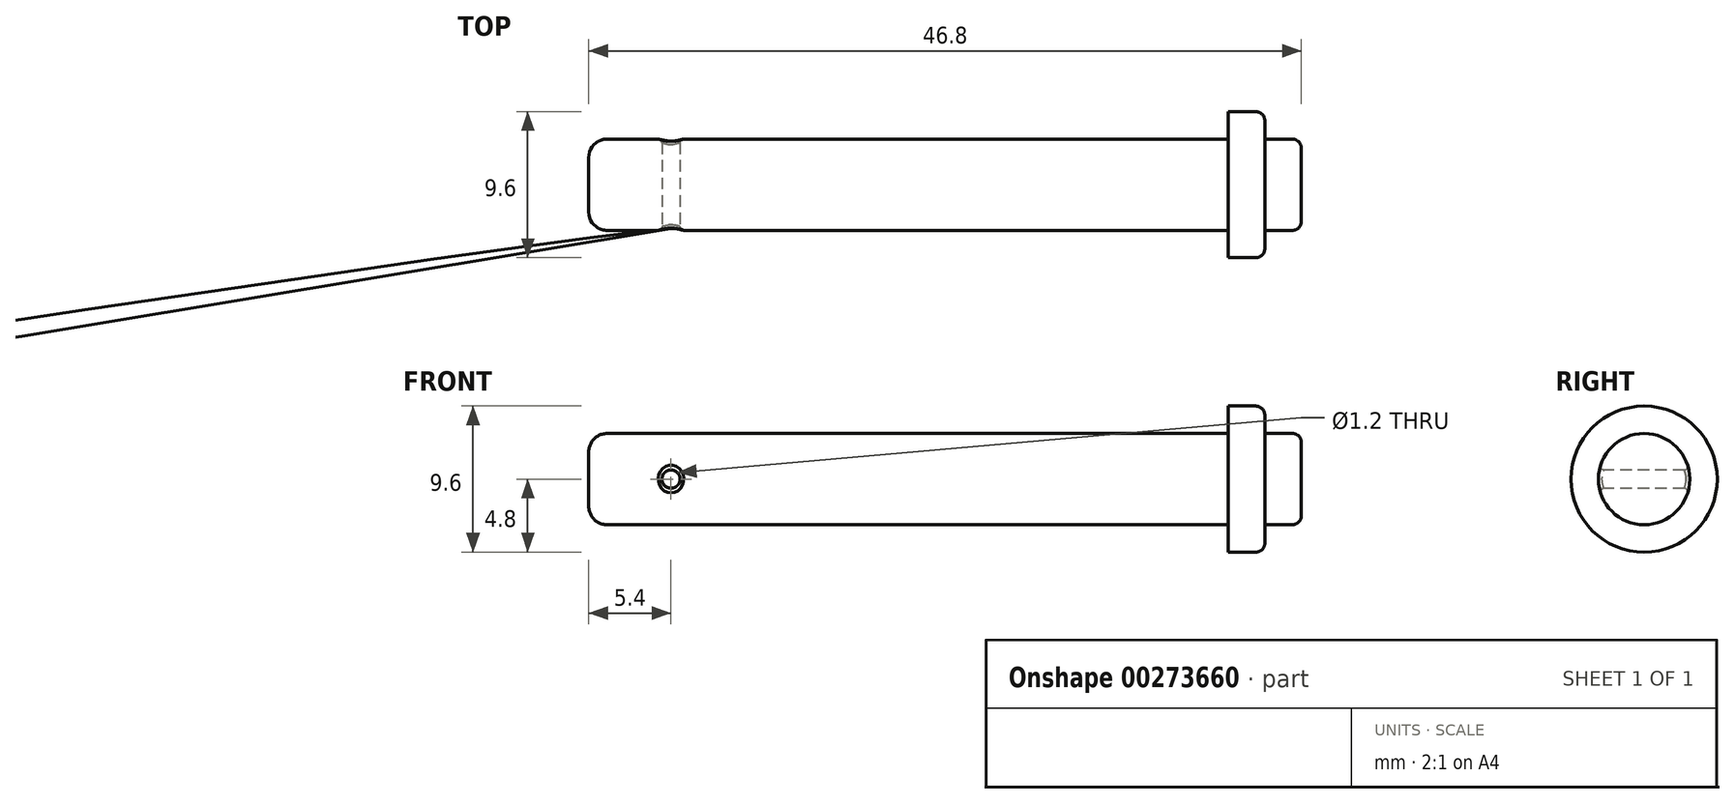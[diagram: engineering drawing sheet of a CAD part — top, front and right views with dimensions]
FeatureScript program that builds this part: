
annotation { "Feature Type Name" : "Feature", "Feature Type Description" : "" }
export const myFeature = defineFeature(function(context is Context, id is Id, definition is map)
    precondition{}
    {
        {
            var Q0;
            Q0=qCreatedBy(makeId("Right.planeOp"),FACE);
            var sketch = newSketch(context, id + "F0", { "sketchPlane" : qUnion([Q0])});
            skCircle(sketch, "E0", {"center": v(0, 0) * mm, "radius": 12.5 * mm});
            skSolve(sketch);
        }
        {
            var Q0;
            Q0=qSketchRegion(id+"F0",true);
            extrude(context, id + "F1", {"entities" : qUnion([Q0]), "depth" : 175 * mm});
        }
        {
            var Q0;
            Q0=makeQuery(id+"F1.opExtrude","CAP_FACE",FACE,{"disambiguationData":[OSD([sQuery(id+"F0.wireOp",EDGE,"E0")])],"isStart":false});
            var sketch = newSketch(context, id + "F2", { "sketchPlane" : qUnion([Q0])});
            skCircle(sketch, "E1", {"center": v(0, 0) * mm, "radius": 20 * mm});
            skSolve(sketch);
        }
        {
            var Q0;
            Q0=qSketchRegion(id+"F2",true);
            extrude(context, id + "F3", {"entities" : qUnion([Q0]), "operationType" : NewBodyOperationType.ADD, "depth" : 10 * mm});
        }
        {
            var Q0;
            Q0=makeQuery(id+"F3.opExtrude","CAP_FACE",FACE,{"disambiguationData":[OSD([sQuery(id+"F2.wireOp",EDGE,"E1")])],"isStart":false});
            var sketch = newSketch(context, id + "F4", { "sketchPlane" : qUnion([Q0])});
            skCircle(sketch, "E2", {"center": v(0, 0) * mm, "radius": 12.5 * mm});
            skSolve(sketch);
        }
        {
            var Q0;
            Q0=makeQuery(id+"F4.imprint","IMPRINT",FACE,{"disambiguationData":[TD([[makeQuery(id+"F4.imprint","IMPRINT",EDGE,{"derivedFrom":sQuery(id+"F4.wireOp",EDGE,"E2")}),1.0]])]});
            extrude(context, id + "F5", {"entities" : qUnion([Q0]), "operationType" : NewBodyOperationType.ADD, "depth" : 10 * mm});
        }
        {
            var Q0;
            Q0=makeQuery(id+"F5.opExtrude","CAP_EDGE",EDGE,{"disambiguationData":[OSD([sQuery(id+"F4.wireOp",EDGE,"E2")])],"isStart":false});
            var Q1;
            Q1=makeQuery(id+"F3.opExtrude","CAP_EDGE",EDGE,{"disambiguationData":[OSD([sQuery(id+"F2.wireOp",EDGE,"E1")])],"isStart":false});
            fillet(context, id + "F6", {"entities" : qUnion([Q0, Q1]), "radius" : 2.5 * mm, "tangentPropagation" : true, "allowEdgeOverflow" : false});
        }
        {
            var Q0;
            Q0=qCreatedBy(makeId("Front.planeOp"),FACE);
            var sketch = newSketch(context, id + "F7", { "sketchPlane" : qUnion([Q0])});
            skCircle(sketch, "E3", {"center": v(22.5, 0) * mm, "radius": 2.5 * mm});
            skSolve(sketch);
        }
        {
            var Q0;
            Q0=qSketchRegion(id+"F7",true);
            extrude(context, id + "F8", {"entities" : qUnion([Q0]), "operationType" : NewBodyOperationType.REMOVE, "endBound" : BoundingType.SYMMETRIC, "oppositeDirection" : true, "depth" : 25 * mm});
        }
        {
            var Q0;
            Q0=makeQuery(id+"F8.boolean.opBoolean","INTERSECT",EDGE,{"disambiguationData":[OD(0.0)],"derivedFrom":[makeQuery(id+"F1.opExtrude","SWEPT_FACE",FACE,{"disambiguationData":[OSD([sQuery(id+"F0.wireOp",EDGE,"E0")])]}),makeQuery(id+"F8.opExtrude","SWEPT_FACE",FACE,{"disambiguationData":[OSD([sQuery(id+"F7.wireOp",EDGE,"E3")])]})]});
            var Q1;
            Q1=makeQuery(id+"F8.boolean.opBoolean","INTERSECT",EDGE,{"disambiguationData":[OD(1.0)],"derivedFrom":[makeQuery(id+"F1.opExtrude","SWEPT_FACE",FACE,{"disambiguationData":[OSD([sQuery(id+"F0.wireOp",EDGE,"E0")])]}),makeQuery(id+"F8.opExtrude","SWEPT_FACE",FACE,{"disambiguationData":[OSD([sQuery(id+"F7.wireOp",EDGE,"E3")])]})]});
            fillet(context, id + "F9", {"entities" : qUnion([Q0, Q1]), "radius" : 1 * mm, "tangentPropagation" : true, "allowEdgeOverflow" : false});
        }
        {
            var Q0;
            Q0=makeQuery(id+"F1.opExtrude","CAP_EDGE",EDGE,{"disambiguationData":[OSD([sQuery(id+"F0.wireOp",EDGE,"E0")])],"isStart":true});
            fillet(context, id + "F10", {"entities" : qUnion([Q0]), "radius" : 5 * mm, "tangentPropagation" : true, "allowEdgeOverflow" : false});
        }
        {
            var Q0;
            Q0=makeQuery(id+"F1.opExtrude","SWEPT_BODY",BODY,{"disambiguationData":[OSD([sQuery(id+"F0.wireOp",EDGE,"E0")])]});
            var Q1;
            Q1=qCreatedBy(makeId("Origin.pointOp"),VERTEX);
            transform(context, id + "F11", {"entities" : qUnion([Q0]), "transformType" : TransformType.SCALE_UNIFORMLY, "scale" : 0.24, "scalePoint" : qUnion([Q1]), "makeCopy" : false});
        }
    });
